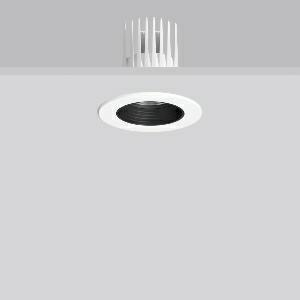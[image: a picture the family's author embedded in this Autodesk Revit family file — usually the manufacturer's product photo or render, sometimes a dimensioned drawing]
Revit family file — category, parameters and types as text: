
# Revit family: heledon_mini_e_901755_002_76_5b70
name_source: partatom
category: Lighting Fixtures
units: mm (PartAtom-declared; Revit-internal decimal feet)

## family parameters
Cut with Voids When Loaded = No
Host = Face
Light Source = No
Part Type = Normal
Room Calculation Point = No
Round Connector Dimension = Use Diameter
Shared = No

## types (1)
- HELEDON mini E (1 x LED Modul 930, 2750 lm, 3000)
    Apparent Load = 29 VA
    Approval mark = CE
    CIE Flux Codes = 95 100 100 100 100
    Color Rendering = 90
    Color Temperature = 3000
    Default Elevation = 1800 mm
    Description = Series: HELEDON mini
Round recessed downlight. Housing: die-cast aluminium, powder-coated. Black plastic ring and recessed LED to prevent glare from the side. Optical assembly with lens made of plastic (polycarbonate) for the best homogeneous light distribution - can be changed without tools. Best colour rendering index Ra>90. Suitable for Recessed ceiling mounting. Installation without tools thanks to spring fastening system. Including separate LED converter with connecting cable 600 mm.High quality converter without flickering and stroboscopic effect. Through-wiring box (5 pole) available as accessory. The following accessories can be mounted without use of tools: interchangeable lenses, decorative glasses, honeycomb louvre, clear and frosted diffusers, white interchangeable plastic ring. 
Colour: traffic white, matt (RAL 9016)
Diameter: 124 mm
Height: 3 mm
Cut-out diameter: 114 mm
Recess height: 170 mm
Luminaire: recess height: 120 mm
Lamp: LED
Socket: without socket
Colour temperature: 3000K
Colour rendering index (CRI): 92
System power: 29 W
Rated luminous flux: 2750 lm
Luminous efficiency: 95 lm/W
Control gear: Converter, dimmable, DALI
Protection class: II
Type of protection: IP 20
    Height = 0 mm  [stored 0 ft]
    Lamp = 1 x LED Modul 930
    Lamp Light Flux = 2750 lm
    Lamp count = 1
    Length = 124 mm  [stored 0.406824 ft]
    Lifetime = 50000 h
    Luminous efficacy = 95 lm/W
    Manufacturer = RZB
    ModVariant = No
    Model = 901755.002.76
    Mounting Place = Ceiling
    Mounting Type = Recessed
    Number of Poles = 1
    OnlyDefault = Yes
    Power Factor = 1
    Product Name = HELEDON mini E
    Product group = Recessed downlights
    ProductGroupID = 402
    Protection Class = Protection class II
    Protection Degree = IP 20
    RLX_Detail_Level = 1
    RLX_Emergency_Light_Flux = 0 lm
    RLX_Emergency_Type = 0
    RLX_Emergency_Type_DB = No
    RlxData = <blob elided: 136957 chars, md5=69fc77e6>
    Socket = socket
    Standby Power = 0 W
    System Light Flux = 2750 lm
    System Power = 29 W
    Type Comments = Product without accessories
    Type Image = 901656.002.jpg
    URL = http://relux.com
    VarID = ---
    Voltage = 230 V
    Voltage Range = 220-240 V
    Weight = 0.00 kg
    Width = 0 mm  [stored 0 ft]

note: [stored X ft] marks values corroborated as IEEE doubles in the binary element streams (Revit-internal decimal feet)

## geometry (parser evidence)
native form markers: Blend x4, Sweep x10
no freeform markers — native parametric forms only
